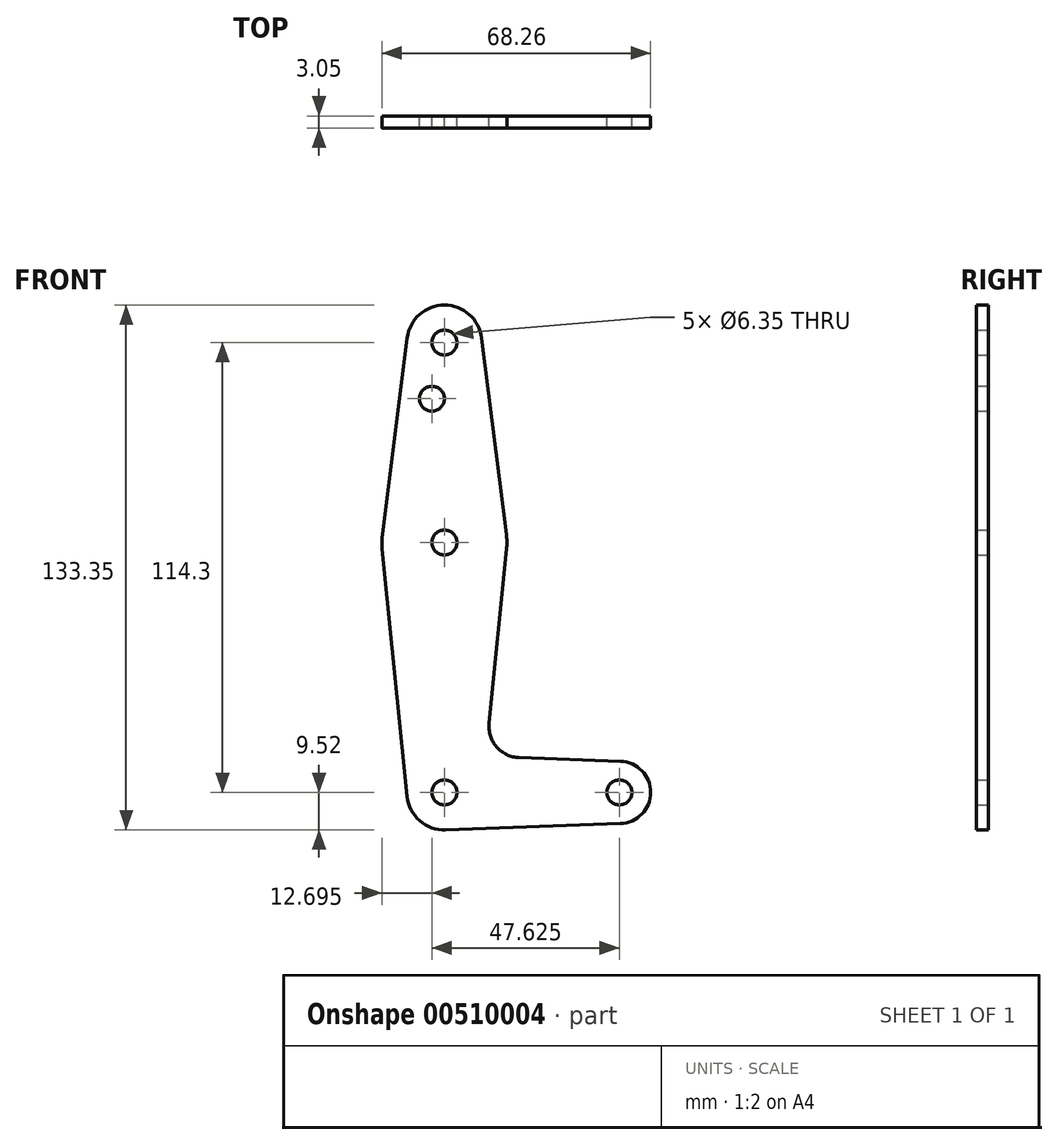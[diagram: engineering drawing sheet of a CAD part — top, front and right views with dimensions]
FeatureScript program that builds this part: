
annotation { "Feature Type Name" : "Feature", "Feature Type Description" : "" }
export const myFeature = defineFeature(function(context is Context, id is Id, definition is map)
    precondition{}
    {
        {
            var Q0;
            Q0=qCreatedBy(makeId("Front.planeOp"),FACE);
            var sketch = newSketch(context, id + "F0", { "sketchPlane" : qUnion([Q0])});
            skLineSegment(sketch, "E0", {"start": v(0, 0) * mm, "end": v(0, 114.3) * mm, "construction": true});
            skLineSegment(sketch, "E1", {"start": v(0, 0) * mm, "end": v(44.45, 0) * mm, "construction": true});
            skCircle(sketch, "E2", {"center": v(0, 0) * mm, "radius": 9.53 * mm});
            skCircle(sketch, "E3", {"center": v(0, 114.3) * mm, "radius": 9.53 * mm});
            skCircle(sketch, "E4", {"center": v(0, 63.5) * mm, "radius": 15.88 * mm});
            skCircle(sketch, "E5", {"center": v(44.45, 0) * mm, "radius": 7.94 * mm});
            skLineSegment(sketch, "E6", {"start": v(-9.45, 115.5) * mm, "end": v(-15.75, 65.48) * mm});
            skLineSegment(sketch, "E7", {"start": v(9.45, 115.5) * mm, "end": v(15.75, 65.48) * mm});
            skLineSegment(sketch, "E8", {"start": v(-15.8, 61.91) * mm, "end": v(-9.48, -0.95) * mm});
            skLineSegment(sketch, "E9", {"start": v(15.8, 61.91) * mm, "end": v(11.34, 17.6) * mm});
            skLineSegment(sketch, "E10", {"start": v(18.97, 8.85) * mm, "end": v(44.73, 7.93) * mm});
            skLineSegment(sketch, "E11", {"start": v(0.34, -9.52) * mm, "end": v(44.73, -7.93) * mm});
            skCircle(sketch, "E12", {"center": v(0, 114.3) * mm, "radius": 3.18 * mm});
            skCircle(sketch, "E13", {"center": v(-3.18, 100.03) * mm, "radius": 3.18 * mm});
            skCircle(sketch, "E14", {"center": v(0, 63.5) * mm, "radius": 3.18 * mm});
            skCircle(sketch, "E15", {"center": v(0, 0) * mm, "radius": 3.18 * mm});
            skCircle(sketch, "E16", {"center": v(44.45, 0) * mm, "radius": 3.18 * mm});
            skArc(sketch, "E17.filletArc", {"start": v(11.34, 17.6) * mm, "mid": v(13.26, 11.57) * mm, "end": v(18.97, 8.85) * mm});
            skSolve(sketch);
        }
        {
            var Q0;
            Q0 = qSketchRegion(id + "F0", true);
            extrude(context, id + "F1", {"entities" : qUnion([Q0]), "depth" : 3.05 * mm});
        }
    });
